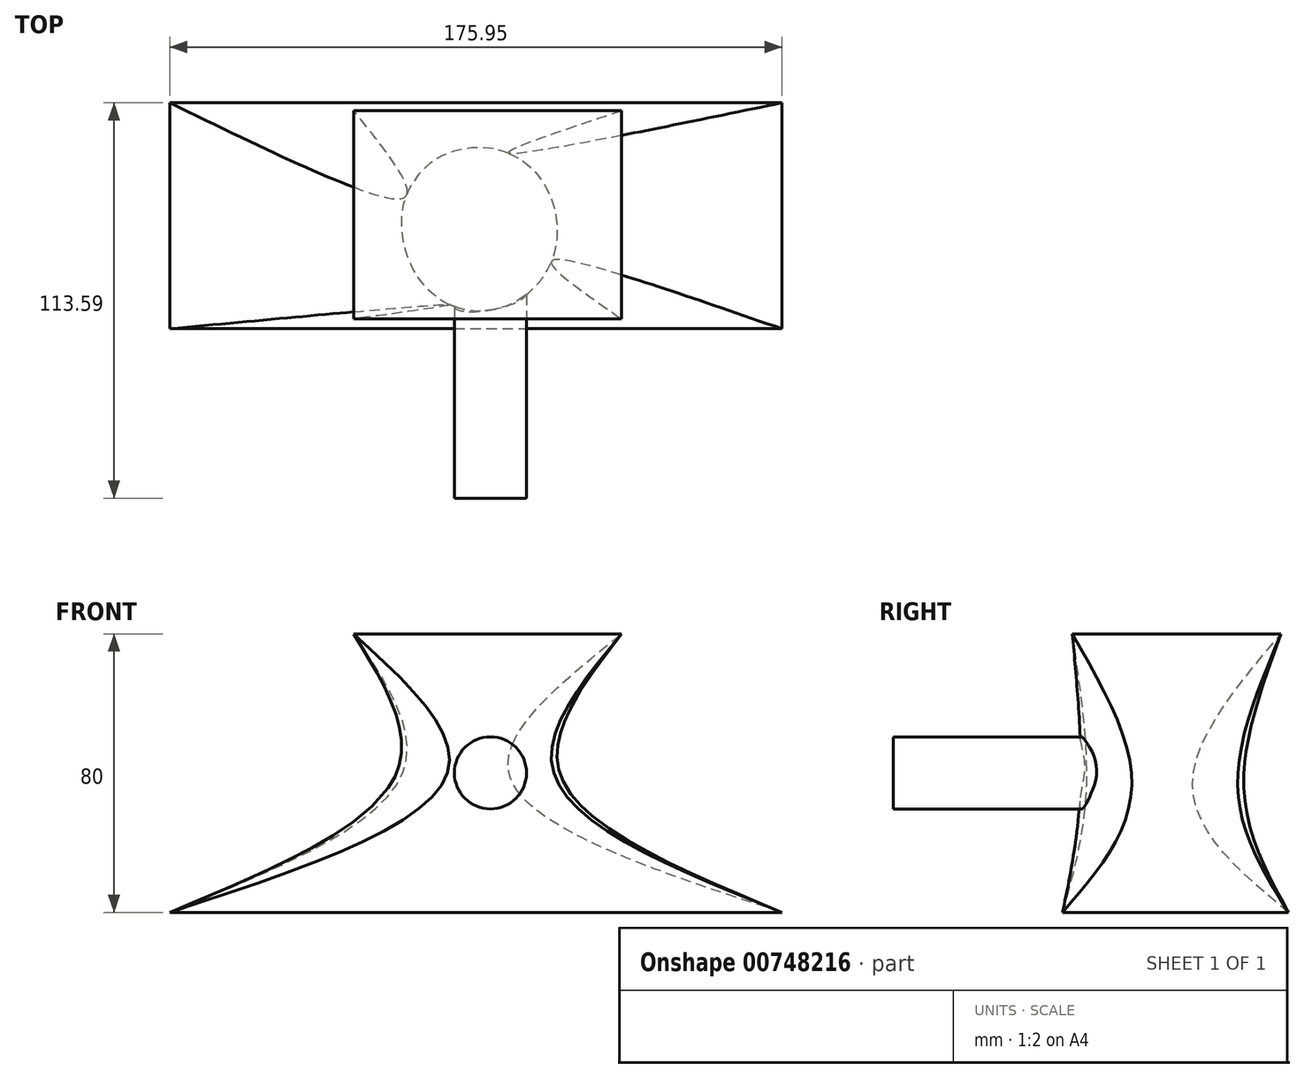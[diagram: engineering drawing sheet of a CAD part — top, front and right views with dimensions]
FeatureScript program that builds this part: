
annotation { "Feature Type Name" : "Feature", "Feature Type Description" : "" }
export const myFeature = defineFeature(function(context is Context, id is Id, definition is map)
    precondition{}
    {
        {
            var Q0;
            Q0=qCreatedBy(makeId("Top.planeOp"),FACE);
            cPlane(context, id + "F0", {"entities" : qUnion([Q0]), "cplaneType" : CPlaneType.OFFSET, "offset" : 40 * mm, "width" : 150 * mm, "height" : 150 * mm});
        }
        {
            var Q0;
            Q0=qCreatedBy(id+"F0.planeOp",FACE);
            cPlane(context, id + "F1", {"entities" : qUnion([Q0]), "cplaneType" : CPlaneType.OFFSET, "offset" : 40 * mm, "width" : 150 * mm, "height" : 150 * mm});
        }
        {
            var Q0;
            Q0=qCreatedBy(makeId("Top.planeOp"),FACE);
            var sketch = newSketch(context, id + "F2", { "sketchPlane" : qUnion([Q0])});
            skLineSegment(sketch, "E0.bottom", {"start": v(-88.68, 33.59) * mm, "end": v(87.27, 33.59) * mm});
            skLineSegment(sketch, "E0.top", {"start": v(-88.68, -31.34) * mm, "end": v(87.27, -31.34) * mm});
            skLineSegment(sketch, "E0.left", {"start": v(-88.68, 33.59) * mm, "end": v(-88.68, -31.34) * mm});
            skLineSegment(sketch, "E0.right", {"start": v(87.27, 33.59) * mm, "end": v(87.27, -31.34) * mm});
            skSolve(sketch);
        }
        {
            var Q0;
            Q0=qCreatedBy(id+"F0.planeOp",FACE);
            var sketch = newSketch(context, id + "F3", { "sketchPlane" : qUnion([Q0])});
            skCircle(sketch, "E1", {"center": v(0, -2.67) * mm, "radius": 23.45 * mm});
            skSolve(sketch);
        }
        {
            var Q0;
            Q0=qCreatedBy(id+"F1.planeOp",FACE);
            var sketch = newSketch(context, id + "F4", { "sketchPlane" : qUnion([Q0])});
            skLineSegment(sketch, "E2.bottom", {"start": v(-35.84, -28.53) * mm, "end": v(41.18, -28.53) * mm});
            skLineSegment(sketch, "E2.top", {"start": v(-35.84, 31.34) * mm, "end": v(41.18, 31.34) * mm});
            skLineSegment(sketch, "E2.left", {"start": v(-35.84, -28.53) * mm, "end": v(-35.84, 31.34) * mm});
            skLineSegment(sketch, "E2.right", {"start": v(41.18, -28.53) * mm, "end": v(41.18, 31.34) * mm});
            skSolve(sketch);
        }
        {
            var Q0;
            Q0=makeQuery(id+"F2.imprint","IMPRINT",FACE,{"disambiguationData":[TD([[makeQuery(id+"F2.imprint","IMPRINT",EDGE,{"derivedFrom":sQuery(id+"F2.wireOp",EDGE,"E0.bottom")}),-1.0]])]});
            var Q1;
            Q1=makeQuery(id+"F3.imprint","IMPRINT",FACE,{"disambiguationData":[TD([[makeQuery(id+"F3.imprint","IMPRINT",EDGE,{"derivedFrom":sQuery(id+"F3.wireOp",EDGE,"E1")}),1.0]])]});
            var Q2;
            Q2=makeQuery(id+"F4.imprint","IMPRINT",FACE,{"disambiguationData":[TD([[makeQuery(id+"F4.imprint","IMPRINT",EDGE,{"derivedFrom":sQuery(id+"F4.wireOp",EDGE,"E2.bottom")}),1.0]])]});
            loft(context, id + "F5", {"sheetProfilesArray" : [{ "sheetProfileEntities" : qUnion([Q0]) }, { "sheetProfileEntities" : qUnion([Q1]) }, { "sheetProfileEntities" : qUnion([Q2]) }]});
        }
        {
            var Q0;
            Q0=qCreatedBy(makeId("Front.planeOp"),FACE);
            cPlane(context, id + "F6", {"entities" : qUnion([Q0]), "cplaneType" : CPlaneType.OFFSET, "offset" : 80 * mm, "width" : 150 * mm, "height" : 150 * mm});
        }
        {
            var Q0;
            Q0=qCreatedBy(id+"F6.planeOp",FACE);
            var sketch = newSketch(context, id + "F7", { "sketchPlane" : qUnion([Q0])});
            skCircle(sketch, "E3", {"center": v(3.51, 40.05) * mm, "radius": 10.37 * mm});
            skSolve(sketch);
        }
        {
            var Q0;
            Q0=makeQuery(id+"F7.imprint","IMPRINT",FACE,{"disambiguationData":[TD([[makeQuery(id+"F7.imprint","IMPRINT",EDGE,{"derivedFrom":sQuery(id+"F7.wireOp",EDGE,"E3")}),1.0]])]});
            extrude(context, id + "F8", {"entities" : qUnion([Q0]), "operationType" : NewBodyOperationType.ADD, "oppositeDirection" : true, "depth" : 63.3 * mm, "offsetDistance" : 25 * mm});
        }
    });
